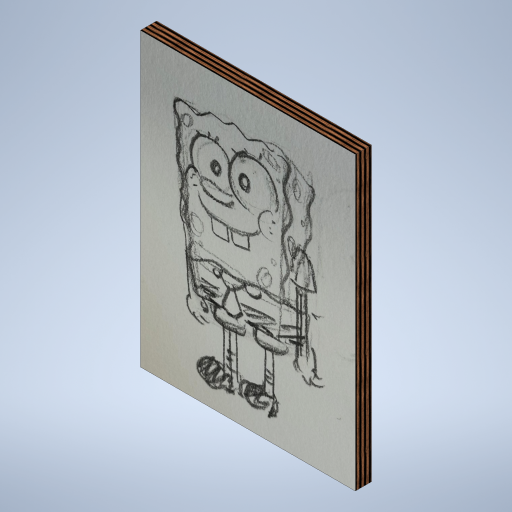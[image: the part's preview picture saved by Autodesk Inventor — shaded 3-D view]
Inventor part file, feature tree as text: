
AUTODESK INVENTOR PART (.ipt)
format: ipt  version: 2023 (Build 270158000, 158)  size: 1,225,728 bytes
history: native  units: in
note: dims shown in document units (in); Inventor stores cm internally (conversion verified against a paired STEP export)
features: extrude x1, sketch x1, other x1
ambient origin geometry x8: Origin, YZ Plane, XZ Plane, XY Plane, X Axis, Y Axis, Z Axis, Center Point
bodies: Solid1 (feature_tree)
feature tree (3):
  extrude  "Extrusion1"  Depth=13.2388in
  sketch  "Sketch1"  dims[d1=1.0in d2=0.0in d3=13.2388in d6=17.9614in]
  other  "Image1"
